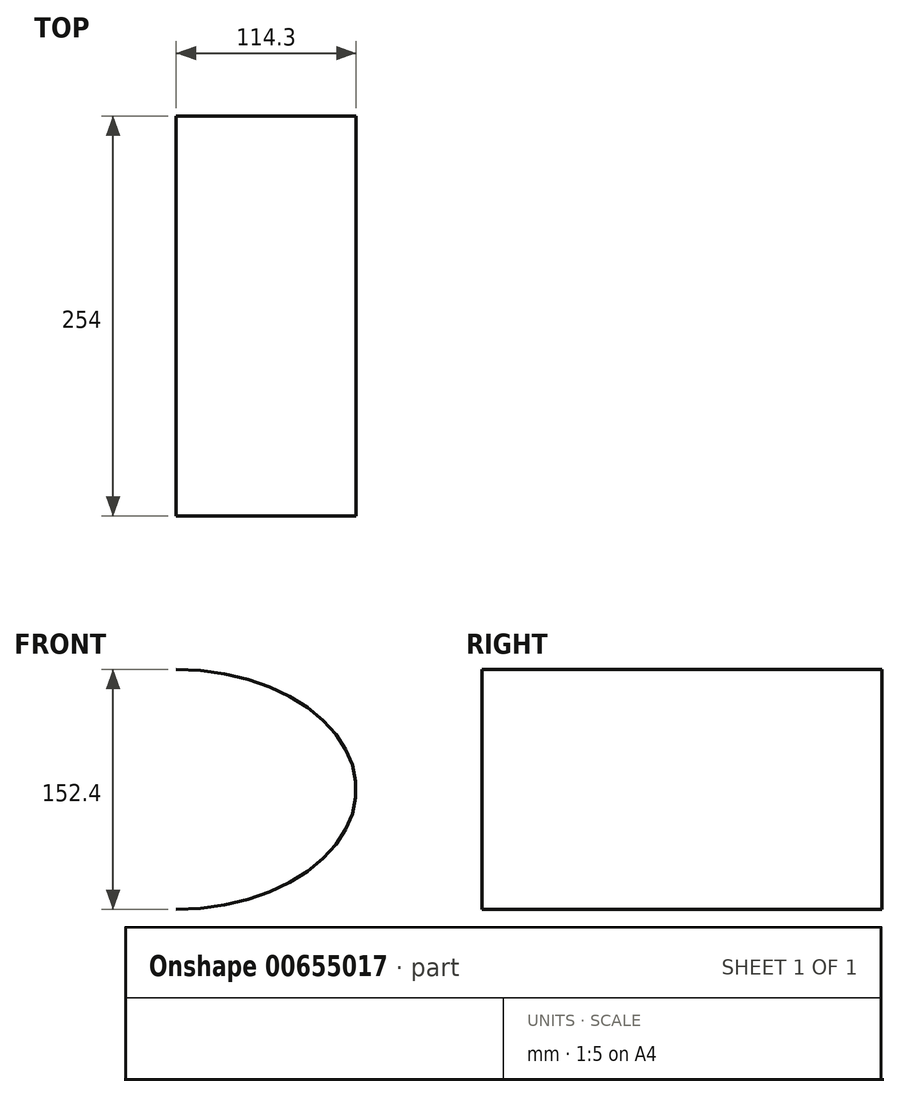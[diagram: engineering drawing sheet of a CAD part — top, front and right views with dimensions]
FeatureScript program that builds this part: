
annotation { "Feature Type Name" : "Feature", "Feature Type Description" : "" }
export const myFeature = defineFeature(function(context is Context, id is Id, definition is map)
    precondition{}
    {
        {
            var Q0;
            Q0=qCreatedBy(makeId("Front.planeOp"),FACE);
            var sketch = newSketch(context, id + "F0", { "sketchPlane" : qUnion([Q0])});
            skEllipticalArc(sketch, "E0", {});
            const initialGuessF0  = {"E0": [0, 0, 1, 0, 0.1143, 0.0762, 4.71238898038469, 1.5707963267948966]};
            skSetInitialGuess(sketch, initialGuessF0);
            skSolve(sketch);
        }
        {
            var Q0;
            Q0=sQuery(id+"F0.wireOp",EDGE,"E0");
            extrude(context, id + "F1", {"bodyType" : ToolBodyType.SURFACE, "surfaceEntities" : qUnion([Q0]), "oppositeDirection" : true, "depth" : 254 * mm, "offsetDistance" : 25.4 * mm});
        }
        {
            var Q0;
            Q0=qCreatedBy(makeId("Right.planeOp"),FACE);
            cPlane(context, id + "F2", {"entities" : qUnion([Q0]), "cplaneType" : CPlaneType.OFFSET, "offset" : 635 * mm, "width" : 152.4 * mm, "height" : 152.4 * mm});
        }
    });
